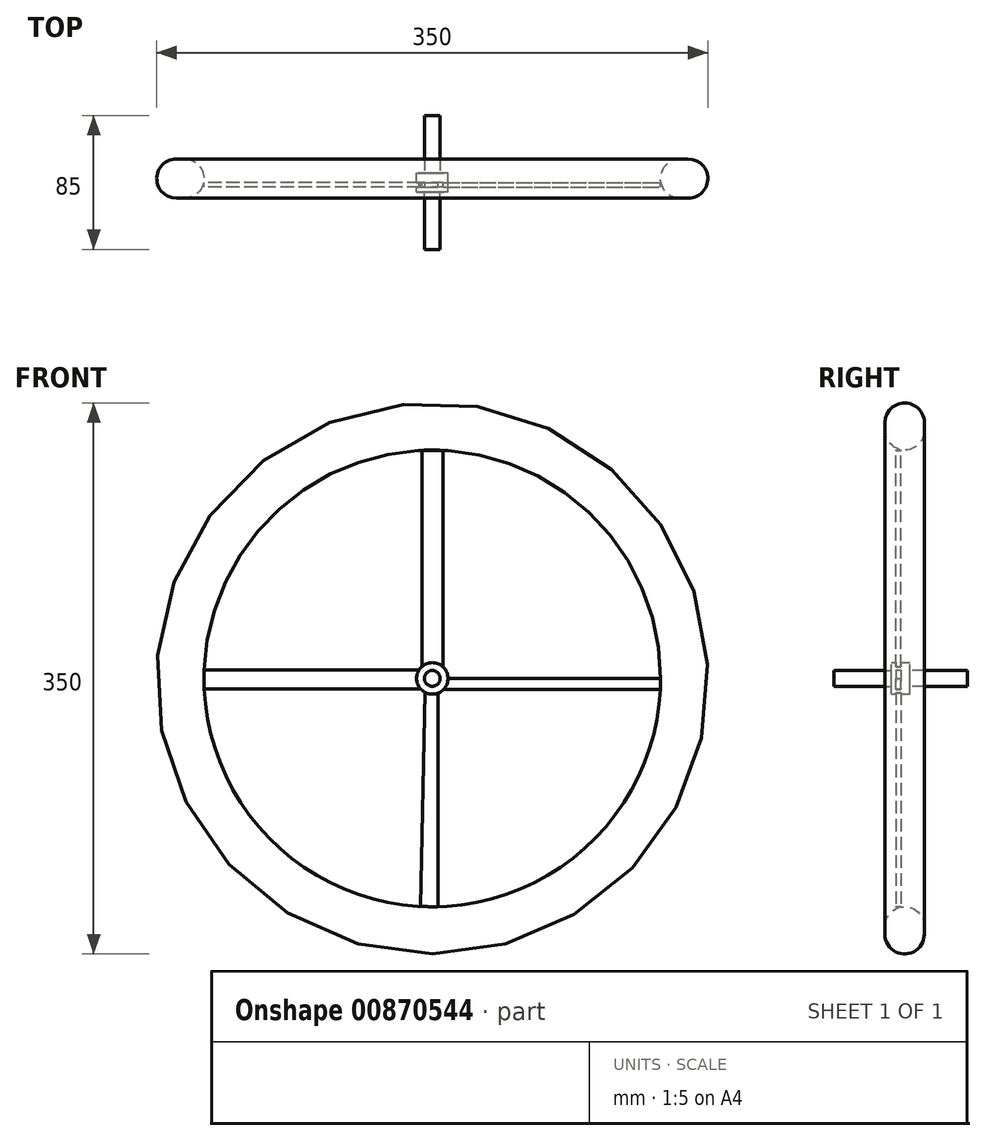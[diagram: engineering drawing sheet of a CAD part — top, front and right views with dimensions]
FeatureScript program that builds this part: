
annotation { "Feature Type Name" : "Feature", "Feature Type Description" : "" }
export const myFeature = defineFeature(function(context is Context, id is Id, definition is map)
    precondition{}
    {
        {
            var Q0;
            Q0=qCreatedBy(makeId("Front.planeOp"),FACE);
            var sketch = newSketch(context, id + "F0", { "sketchPlane" : qUnion([Q0])});
            skCircle(sketch, "E0", {"center": v(0, 0) * mm, "radius": 145 * mm});
            skCircle(sketch, "E1", {"center": v(0, 0) * mm, "radius": 175 * mm});
            skCircle(sketch, "E2", {"center": v(0, 0) * mm, "radius": 5 * mm});
            skCircle(sketch, "E3", {"center": v(0, 0) * mm, "radius": 10 * mm});
            skLineSegment(sketch, "E4", {"start": v(-10, 0) * mm, "end": v(-145, 0) * mm});
            skLineSegment(sketch, "E5", {"start": v(10, 0) * mm, "end": v(145, 0) * mm});
            skLineSegment(sketch, "E6", {"start": v(0, 10) * mm, "end": v(0, 145) * mm});
            skLineSegment(sketch, "E7", {"start": v(0, -10) * mm, "end": v(0, -145) * mm});
            skLineSegment(sketch, "E8", {"start": v(7.1, -7.03) * mm, "end": v(144.83, -7.03) * mm});
            skLineSegment(sketch, "E9", {"start": v(-7.45, -6.67) * mm, "end": v(-144.85, -6.67) * mm});
            skLineSegment(sketch, "E10", {"start": v(-6.48, 7.61) * mm, "end": v(-6.48, 144.86) * mm});
            skLineSegment(sketch, "E11", {"start": v(6.92, 7.21) * mm, "end": v(6.92, 144.83) * mm});
            skLineSegment(sketch, "E12", {"start": v(-8.4, 5.43) * mm, "end": v(-144.9, 5.43) * mm});
            skLineSegment(sketch, "E13", {"start": v(-4.78, -8.78) * mm, "end": v(-7.45, -144.8) * mm});
            skLineSegment(sketch, "E14", {"start": v(3.76, -9.26) * mm, "end": v(3.76, -144.95) * mm});
            skSolve(sketch);
        }
        {
            var Q0;
            Q0=makeQuery(id+"F0.imprint","IMPRINT",FACE,{"disambiguationData":[TD([[makeQuery(id+"F0.imprint","IMPRINT",EDGE,{"derivedFrom":sQuery(id+"F0.wireOp",EDGE,"E1")}),1.0]])]});
            extrude(context, id + "F1", {"entities" : qUnion([Q0]), "depth" : 10 * mm, "offsetDistance" : 25 * mm});
        }
        {
            var Q0;
            Q0=makeQuery(id+"F0.imprint","IMPRINT",FACE,{"disambiguationData":[TD([[makeQuery(id+"F0.imprint","IMPRINT",EDGE,{"derivedFrom":sQuery(id+"F0.wireOp",EDGE,"E2")}),-1.0]])]});
            extrude(context, id + "F2", {"entities" : qUnion([Q0]), "operationType" : NewBodyOperationType.ADD, "depth" : 6 * mm, "offsetDistance" : 25 * mm});
        }
        {
            var Q0;
            Q0=makeQuery(id+"F0.imprint","IMPRINT",FACE,{"disambiguationData":[TD([[makeQuery(id+"F0.imprint","IMPRINT",EDGE,{"derivedFrom":sQuery(id+"F0.wireOp",EDGE,"E2")}),1.0]])]});
            extrude(context, id + "F3", {"entities" : qUnion([Q0]), "operationType" : NewBodyOperationType.ADD, "depth" : 42.5 * mm, "offsetDistance" : 25 * mm});
        }
        {
            var Q0;
            Q0=makeQuery(id+"F0.imprint","IMPRINT",FACE,{"disambiguationData":[TD([[makeQuery(id+"F0.imprint","IMPRINT",EDGE,{"derivedFrom":sQuery(id+"F0.wireOp",EDGE,"E2")}),1.0]])]});
            var sketch = newSketch(context, id + "F4", { "sketchPlane" : qUnion([Q0])});
            skCircle(sketch, "E15", {"center": v(0, 0) * mm, "radius": 5 * mm});
            skCircle(sketch, "E16", {"center": v(0, 0) * mm, "radius": 175 * mm});
            skCircle(sketch, "E17", {"center": v(0, 0) * mm, "radius": 145 * mm});
            skCircle(sketch, "E18", {"center": v(0, 0) * mm, "radius": 10 * mm});
            skSolve(sketch);
        }
        {
            var Q0;
            Q0=makeQuery(id+"F4.imprint","IMPRINT",FACE,{"disambiguationData":[TD([[makeQuery(id+"F4.imprint","IMPRINT",EDGE,{"derivedFrom":sQuery(id+"F4.wireOp",EDGE,"E15")}),1.0]])]});
            extrude(context, id + "F5", {"entities" : qUnion([Q0]), "operationType" : NewBodyOperationType.ADD, "depth" : -42.5 * mm, "offsetDistance" : 25 * mm});
        }
        {
            var Q0;
            Q0=makeQuery(id+"F0.imprint","IMPRINT",FACE,{"disambiguationData":[TD([[makeQuery(id+"F0.imprint","IMPRINT",EDGE,{"derivedFrom":sQuery(id+"F0.wireOp",EDGE,"E1")}),1.0]])]});
            extrude(context, id + "F6", {"entities" : qUnion([Q0]), "operationType" : NewBodyOperationType.ADD, "depth" : -15 * mm, "offsetDistance" : 25 * mm});
        }
        {
            var Q0;
            Q0=makeQuery(id+"F0.imprint","IMPRINT",FACE,{"disambiguationData":[TD([[makeQuery(id+"F0.imprint","IMPRINT",EDGE,{"derivedFrom":sQuery(id+"F0.wireOp",EDGE,"E2")}),-1.0]])]});
            extrude(context, id + "F7", {"entities" : qUnion([Q0]), "operationType" : NewBodyOperationType.ADD, "depth" : -6 * mm, "offsetDistance" : 25 * mm});
        }
        {
            var Q0;
            {var subQ0=sQuery(id+"F0.wireOp",EDGE,"E1");Q0=makeQuery(id+"F6.boolean.opBoolean","MERGE",FACE,{"derivedFrom":[makeQuery(id+"F1.opExtrude","SWEPT_FACE",FACE,{"disambiguationData":[OSD([subQ0])]}),makeQuery(id+"F6.opExtrude","SWEPT_FACE",FACE,{"disambiguationData":[OSD([subQ0])]})]});}
            fillet(context, id + "F8", {"entities" : qUnion([Q0]), "radius" : 12.5 * mm, "tangentPropagation" : true, "allowEdgeOverflow" : false});
        }
        {
            var Q0;
            Q0=makeQuery(id+"F1.opExtrude","CAP_EDGE",EDGE,{"disambiguationData":[OSD([sQuery(id+"F0.wireOp",EDGE,"E0")])],"isStart":false});
            fillet(context, id + "F9", {"entities" : qUnion([Q0]), "radius" : 12.5 * mm, "tangentPropagation" : true, "allowEdgeOverflow" : false});
        }
        {
            var Q0;
            Q0=makeQuery(id+"F6.opExtrude","CAP_EDGE",EDGE,{"disambiguationData":[OSD([sQuery(id+"F0.wireOp",EDGE,"E0")])],"isStart":false});
            fillet(context, id + "F10", {"entities" : qUnion([Q0]), "radius" : 12.5 * mm, "tangentPropagation" : true, "allowEdgeOverflow" : false});
        }
        {
            var Q0;
            {var subQ0=sQuery(id+"F0.wireOp",EDGE,"E6");Q0=makeQuery(id+"F0.imprint","IMPRINT",FACE,{"disambiguationData":[TD([[makeQuery(id+"F0.imprint","IMPRINT",EDGE,{"derivedFrom":subQ0}),-1.0]])]});}
            var Q1;
            {var subQ0=sQuery(id+"F0.wireOp",EDGE,"E6");Q1=makeQuery(id+"F0.imprint","IMPRINT",FACE,{"disambiguationData":[TD([[makeQuery(id+"F0.imprint","IMPRINT",EDGE,{"derivedFrom":subQ0}),1.0]])]});}
            var Q2;
            {var subQ0=sQuery(id+"F0.wireOp",EDGE,"E4");Q2=makeQuery(id+"F0.imprint","IMPRINT",FACE,{"disambiguationData":[TD([[makeQuery(id+"F0.imprint","IMPRINT",EDGE,{"derivedFrom":subQ0}),-1.0]])]});}
            var Q3;
            {var subQ0=sQuery(id+"F0.wireOp",EDGE,"E4");Q3=makeQuery(id+"F0.imprint","IMPRINT",FACE,{"disambiguationData":[TD([[makeQuery(id+"F0.imprint","IMPRINT",EDGE,{"derivedFrom":subQ0}),1.0]])]});}
            var Q4;
            {var subQ0=sQuery(id+"F0.wireOp",EDGE,"E7");Q4=makeQuery(id+"F0.imprint","IMPRINT",FACE,{"disambiguationData":[TD([[makeQuery(id+"F0.imprint","IMPRINT",EDGE,{"derivedFrom":subQ0}),-1.0]])]});}
            var Q5;
            {var subQ0=sQuery(id+"F0.wireOp",EDGE,"E7");Q5=makeQuery(id+"F0.imprint","IMPRINT",FACE,{"disambiguationData":[TD([[makeQuery(id+"F0.imprint","IMPRINT",EDGE,{"derivedFrom":subQ0}),1.0]])]});}
            var Q6;
            {var subQ0=sQuery(id+"F0.wireOp",EDGE,"E5");Q6=makeQuery(id+"F0.imprint","IMPRINT",FACE,{"disambiguationData":[TD([[makeQuery(id+"F0.imprint","IMPRINT",EDGE,{"derivedFrom":subQ0}),-1.0]])]});}
            extrude(context, id + "F11", {"entities" : qUnion([Q0, Q1, Q2, Q3, Q4, Q5, Q6]), "operationType" : NewBodyOperationType.ADD, "depth" : 3 * mm, "offsetDistance" : 25 * mm});
        }
    });
